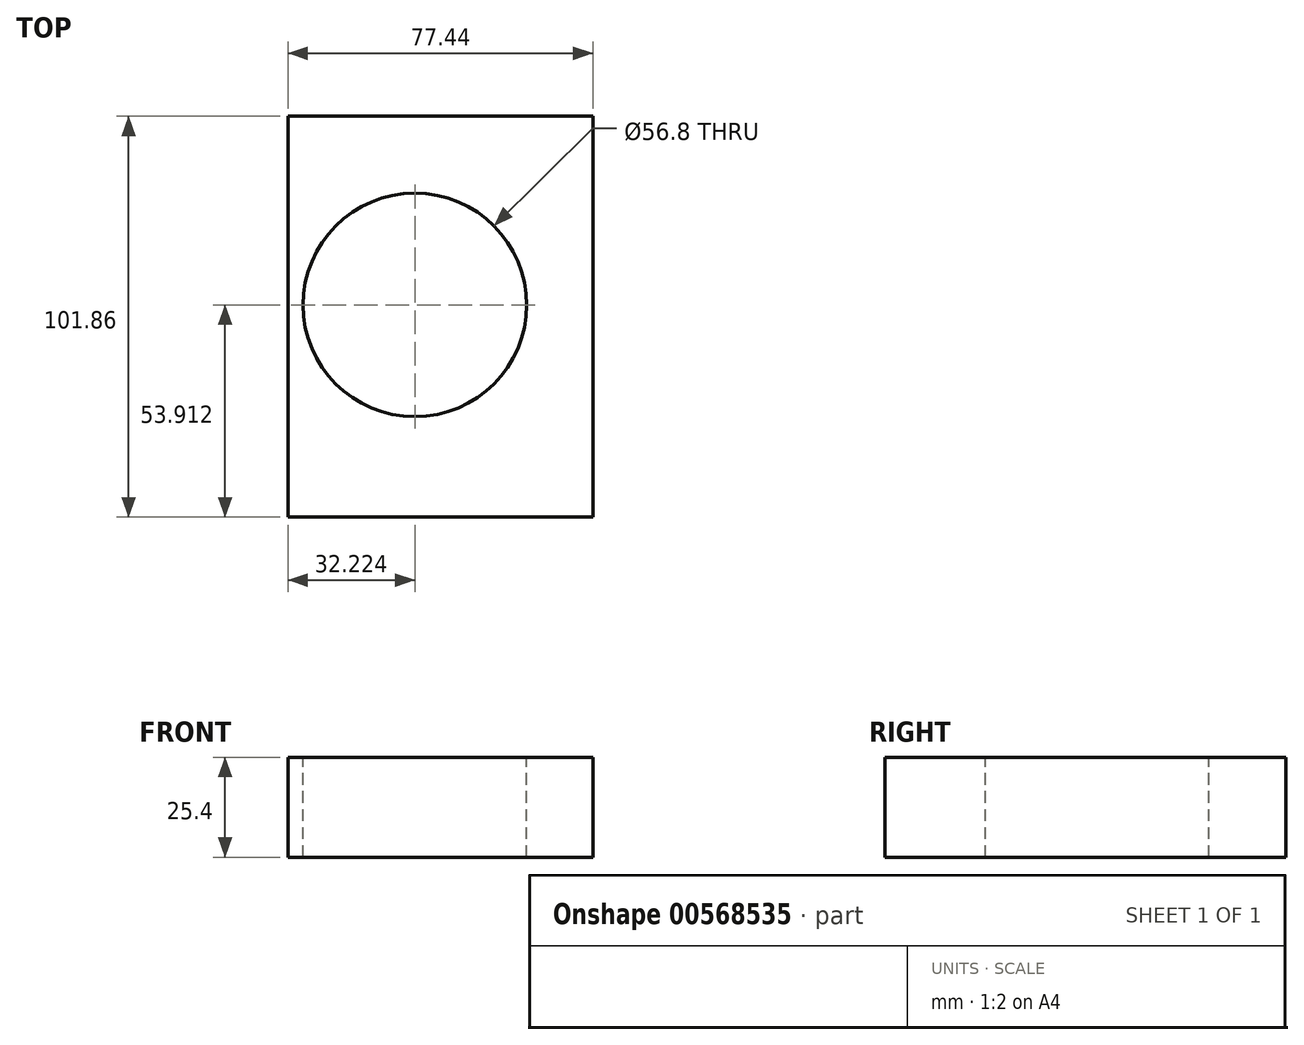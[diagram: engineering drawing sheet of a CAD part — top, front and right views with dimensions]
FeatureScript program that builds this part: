
annotation { "Feature Type Name" : "Feature", "Feature Type Description" : "" }
export const myFeature = defineFeature(function(context is Context, id is Id, definition is map)
    precondition{}
    {
        {
            var Q0;
            Q0=qCreatedBy(makeId("Top.planeOp"),FACE);
            var sketch = newSketch(context, id + "F0", { "sketchPlane" : qUnion([Q0])});
            skLineSegment(sketch, "E0.bottom", {"start": v(-102.22, 47.21) * mm, "end": v(-24.78, 47.21) * mm});
            skLineSegment(sketch, "E0.top", {"start": v(-102.22, -54.65) * mm, "end": v(-24.78, -54.65) * mm});
            skLineSegment(sketch, "E0.left", {"start": v(-102.22, 47.21) * mm, "end": v(-102.22, -54.65) * mm});
            skLineSegment(sketch, "E0.right", {"start": v(-24.78, 47.21) * mm, "end": v(-24.78, -54.65) * mm});
            skSolve(sketch);
        }
        {
            var Q0;
            Q0 = qSketchRegion(id + "F0", true);
            extrude(context, id + "F1", {"entities" : qUnion([Q0]), "depth" : 25.4 * mm, "offsetDistance" : 25.4 * mm});
        }
        {
            var Q0;
            Q0=makeQuery(id+"F1.opExtrude","CAP_FACE",FACE,{"disambiguationData":[OSD([sQuery(id+"F0.wireOp",EDGE,"E0.bottom"),sQuery(id+"F0.wireOp",EDGE,"E0.top"),sQuery(id+"F0.wireOp",EDGE,"E0.left"),sQuery(id+"F0.wireOp",EDGE,"E0.right")])],"isStart":false});
            var sketch = newSketch(context, id + "F2", { "sketchPlane" : qUnion([Q0])});
            skCircle(sketch, "E1", {"center": v(-70, -0.74) * mm, "radius": 28.4 * mm});
            skSolve(sketch);
        }
        {
            var Q0;
            Q0 = qSketchRegion(id + "F2", true);
            extrude(context, id + "F3", {"entities" : qUnion([Q0]), "operationType" : NewBodyOperationType.REMOVE, "oppositeDirection" : true, "depth" : 25.4 * mm, "offsetDistance" : 25.4 * mm});
        }
    });
